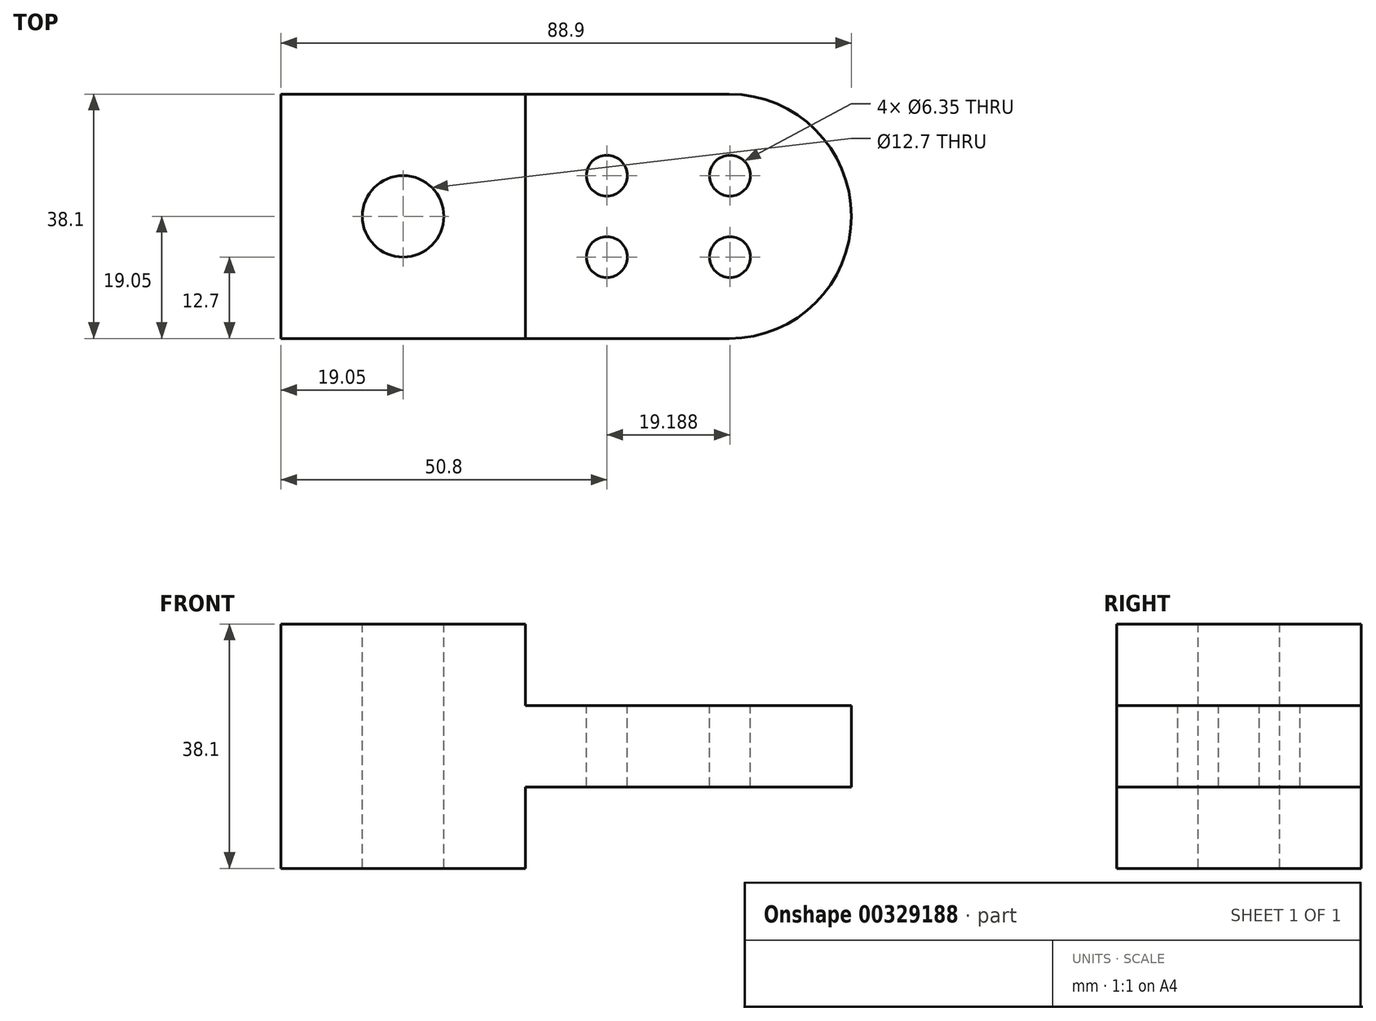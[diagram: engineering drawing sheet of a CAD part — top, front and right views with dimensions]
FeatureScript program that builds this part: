
annotation { "Feature Type Name" : "Feature", "Feature Type Description" : "" }
export const myFeature = defineFeature(function(context is Context, id is Id, definition is map)
    precondition{}
    {
        {
            var Q0;
            Q0=qCreatedBy(makeId("Top.planeOp"),FACE);
            var sketch = newSketch(context, id + "F0", { "sketchPlane" : qUnion([Q0])});
            skLineSegment(sketch, "E0.left", {"start": v(0, 0) * mm, "end": v(0, 38.1) * mm});
            skLineSegment(sketch, "E1", {"start": v(88.9, 19.05) * mm, "end": v(69.85, 19.05) * mm, "construction": true});
            skLineSegment(sketch, "E2", {"start": v(0, 38.1) * mm, "end": v(69.85, 38.1) * mm});
            skLineSegment(sketch, "E3", {"start": v(0, 0) * mm, "end": v(69.85, 0) * mm});
            skArc(sketch, "E4", {"start": v(69.85, 38.1) * mm, "mid": v(88.9, 19.05) * mm, "end": v(69.85, 0) * mm});
            skSolve(sketch);
        }
        {
            var Q0;
            Q0 = qSketchRegion(id + "F0", true);
            extrude(context, id + "F1", {"entities" : qUnion([Q0]), "depth" : 38.1 * mm});
        }
        {
            var Q0;
            Q0=makeQuery(id+"F1.opExtrude","SWEPT_FACE",FACE,{"disambiguationData":[OSD([sQuery(id+"F0.wireOp",EDGE,"E3")])]});
            var sketch = newSketch(context, id + "F2", { "sketchPlane" : qUnion([Q0])});
            skLineSegment(sketch, "E5", {"start": v(88.9, 25.4) * mm, "end": v(88.9, 12.7) * mm});
            skLineSegment(sketch, "E6", {"start": v(88.9, 25.4) * mm, "end": v(38.1, 25.4) * mm});
            skLineSegment(sketch, "E7", {"start": v(88.9, 12.7) * mm, "end": v(38.1, 12.7) * mm});
            skLineSegment(sketch, "E8", {"start": v(38.1, 12.7) * mm, "end": v(38.1, 0) * mm});
            skLineSegment(sketch, "E9", {"start": v(38.1, 25.4) * mm, "end": v(38.1, 38.1) * mm});
            skLineSegment(sketch, "E10", {"start": v(38.1, 38.1) * mm, "end": v(88.9, 38.1) * mm});
            skLineSegment(sketch, "E11", {"start": v(88.9, 38.1) * mm, "end": v(88.9, 25.4) * mm});
            skLineSegment(sketch, "E12", {"start": v(38.1, 0) * mm, "end": v(88.9, 0) * mm});
            skLineSegment(sketch, "E13", {"start": v(88.9, 0) * mm, "end": v(88.9, 12.7) * mm});
            skSolve(sketch);
        }
        {
            var Q0;
            Q0 = qSketchRegion(id + "F2", true);
            extrude(context, id + "F3", {"entities" : qUnion([Q0]), "operationType" : NewBodyOperationType.REMOVE, "endBound" : BoundingType.THROUGH_ALL, "oppositeDirection" : true, "depth" : 25.4 * mm});
        }
        {
            var Q0;
            Q0=makeQuery(id+"F1.opExtrude","CAP_FACE",FACE,{"disambiguationData":[OSD([sQuery(id+"F0.wireOp",EDGE,"E0.left"),sQuery(id+"F0.wireOp",EDGE,"E2"),sQuery(id+"F0.wireOp",EDGE,"E3"),sQuery(id+"F0.wireOp",EDGE,"E4")])],"isStart":false});
            var sketch = newSketch(context, id + "F4", { "sketchPlane" : qUnion([Q0])});
            skCircle(sketch, "E14", {"center": v(19.05, 19.05) * mm, "radius": 6.35 * mm});
            skCircle(sketch, "E15", {"center": v(50.8, 25.4) * mm, "radius": 3.18 * mm});
            skCircle(sketch, "E16", {"center": v(50.8, 12.7) * mm, "radius": 3.18 * mm});
            skCircle(sketch, "E17", {"center": v(69.99, 25.4) * mm, "radius": 3.18 * mm});
            skCircle(sketch, "E18", {"center": v(69.99, 12.7) * mm, "radius": 3.18 * mm});
            skPoint(sketch, "E19.0.1.end.orphan", {"position": v(38.1, 38.1) * mm});
            skPoint(sketch, "E19.0.0.start.orphan", {"position": v(69.85, 38.1) * mm});
            skPoint(sketch, "E19.0.3.end.orphan", {"position": v(69.85, 0) * mm});
            skPoint(sketch, "E19.0.3.start.orphan", {"position": v(38.1, 0) * mm});
            skSolve(sketch);
        }
        {
            var Q0;
            Q0 = qSketchRegion(id + "F4", true);
            extrude(context, id + "F5", {"entities" : qUnion([Q0]), "operationType" : NewBodyOperationType.REMOVE, "endBound" : BoundingType.THROUGH_ALL, "oppositeDirection" : true, "depth" : 25.4 * mm});
        }
    });
